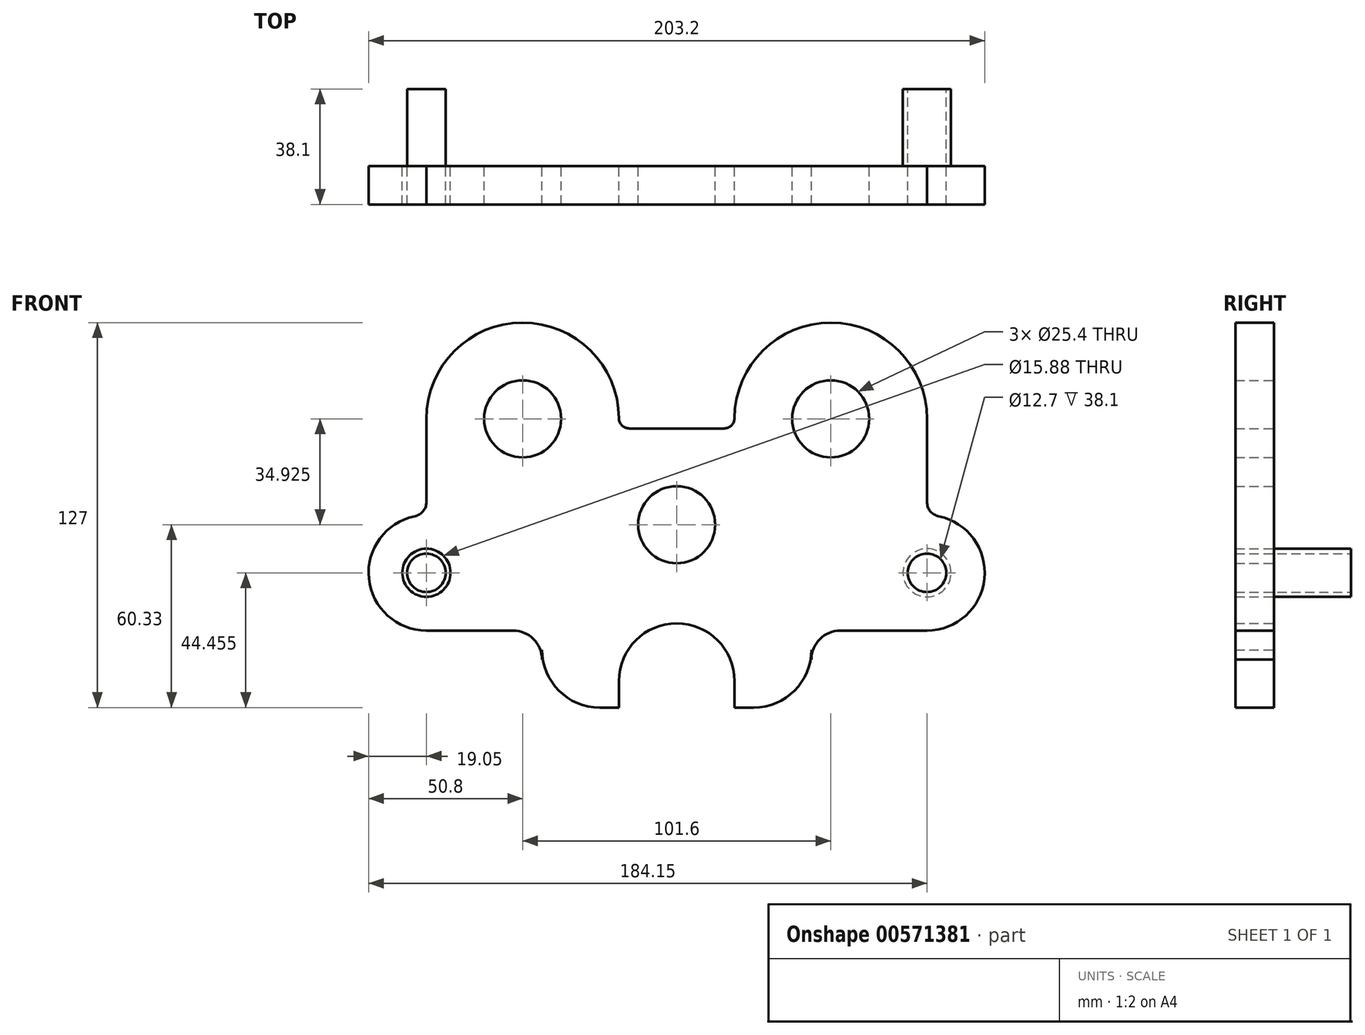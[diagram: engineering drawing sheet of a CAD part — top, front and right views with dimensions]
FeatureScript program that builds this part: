
annotation { "Feature Type Name" : "Feature", "Feature Type Description" : "" }
export const myFeature = defineFeature(function(context is Context, id is Id, definition is map)
    precondition{}
    {
        {
            var Q0;
            Q0=qCreatedBy(makeId("Front.planeOp"),FACE);
            var sketch = newSketch(context, id + "F0", { "sketchPlane" : qUnion([Q0])});
            skArc(sketch, "E0", {"start": v(82.55, 34.93) * mm, "mid": v(50.9, 66.67) * mm, "end": v(19.05, 35.12) * mm});
            skLineSegment(sketch, "E1", {"start": v(82.55, 34.93) * mm, "end": v(82.55, 7.46) * mm});
            skArc(sketch, "E2", {"start": v(82.55, -34.92) * mm, "mid": v(101.5, -17.79) * mm, "end": v(86.36, 2.8) * mm});
            skLineSegment(sketch, "E3", {"start": v(82.55, -34.92) * mm, "end": v(53.98, -34.92) * mm});
            skCircle(sketch, "E4", {"center": v(50.8, 34.93) * mm, "radius": 12.7 * mm});
            skCircle(sketch, "E5", {"center": v(82.55, -15.87) * mm, "radius": 6.35 * mm});
            skLineSegment(sketch, "E6", {"start": v(50.8, 74.41) * mm, "end": v(50.8, -7.1) * mm, "construction": true});
            skPoint(sketch, "E6.startSnap0", {"position": v(50.8, 66.67) * mm});
            skLineSegment(sketch, "E7", {"start": v(72.24, 34.93) * mm, "end": v(7.49, 34.93) * mm, "construction": true});
            skLineSegment(sketch, "E8", {"start": v(82.55, 0) * mm, "end": v(82.55, -56.09) * mm, "construction": true});
            skLineSegment(sketch, "E9", {"start": v(38.27, -15.87) * mm, "end": v(117.37, -15.87) * mm, "construction": true});
            skCircle(sketch, "E10", {"center": v(0, 0) * mm, "radius": 12.7 * mm});
            skLineSegment(sketch, "E11", {"start": v(0, 42.71) * mm, "end": v(0, -64.9) * mm, "construction": true});
            skLineSegment(sketch, "E12", {"start": v(-44.82, 0) * mm, "end": v(29.18, 0) * mm, "construction": true});
            skPoint(sketch, "E13.orphan", {"position": v(0, 34.92) * mm});
            skLineSegment(sketch, "E14", {"start": v(0, 31.75) * mm, "end": v(15.66, 31.75) * mm});
            skLineSegment(sketch, "E15", {"start": v(44.45, -41.27) * mm, "end": v(44.45, -44.45) * mm});
            skLineSegment(sketch, "E16", {"start": v(25.4, -60.32) * mm, "end": v(19.05, -60.32) * mm});
            skLineSegment(sketch, "E17", {"start": v(19.05, -60.32) * mm, "end": v(19.05, -51.59) * mm});
            skPoint(sketch, "E18.visualSharp", {"position": v(19.05, -32.6) * mm});
            skPoint(sketch, "E19.visualSharp", {"position": v(44.45, -60.32) * mm});
            skArc(sketch, "E19.filletArc", {"start": v(25.4, -60.32) * mm, "mid": v(38.87, -54.75) * mm, "end": v(44.45, -41.27) * mm});
            skPoint(sketch, "E20.visualSharp", {"position": v(44.45, -34.92) * mm});
            skArc(sketch, "E20.filletArc", {"start": v(53.98, -34.92) * mm, "mid": v(47.24, -37.71) * mm, "end": v(44.45, -44.45) * mm});
            skPoint(sketch, "E21.visualSharp", {"position": v(82.55, 3.17) * mm});
            skArc(sketch, "E21.filletArc", {"start": v(82.55, 7.46) * mm, "mid": v(83.62, 4.44) * mm, "end": v(86.36, 2.8) * mm});
            skPoint(sketch, "E22.newPointA", {"position": v(19.05, 34.92) * mm});
            skPoint(sketch, "E22.newPointB", {"position": v(7.49, 31.75) * mm});
            skArc(sketch, "E22.filletArc", {"start": v(15.66, 31.75) * mm, "mid": v(18.05, 32.73) * mm, "end": v(19.05, 35.12) * mm});
            skLineSegment(sketch, "E23", {"start": v(-60.5, -47.62) * mm, "end": v(83.9, -47.62) * mm, "construction": true});
            skLineSegment(sketch, "E24.MirrorCS", {"start": v(0, 31.75) * mm, "end": v(-15.66, 31.75) * mm});
            skPoint(sketch, "E25.MirrorP", {"position": v(-7.49, 31.75) * mm});
            skPoint(sketch, "E26.MirrorP", {"position": v(-19.05, 34.92) * mm});
            skArc(sketch, "E27.MirrorCS", {"start": v(-82.55, 34.93) * mm, "mid": v(-50.9, 66.67) * mm, "end": v(-19.05, 35.12) * mm});
            skLineSegment(sketch, "E28.MirrorCS", {"start": v(-82.55, 34.93) * mm, "end": v(-82.55, 7.46) * mm});
            skArc(sketch, "E29.MirrorCS", {"start": v(-82.55, -34.92) * mm, "mid": v(-101.5, -17.79) * mm, "end": v(-86.36, 2.8) * mm});
            skLineSegment(sketch, "E30.MirrorCS", {"start": v(-82.55, -34.93) * mm, "end": v(-53.98, -34.92) * mm});
            skArc(sketch, "E31.MirrorCS", {"start": v(-25.4, -60.32) * mm, "mid": v(-38.87, -54.75) * mm, "end": v(-44.45, -41.27) * mm});
            skLineSegment(sketch, "E32.MirrorCS", {"start": v(-25.4, -60.32) * mm, "end": v(-19.05, -60.32) * mm});
            skLineSegment(sketch, "E33.MirrorCS", {"start": v(-19.05, -60.32) * mm, "end": v(-19.05, -51.59) * mm});
            skPoint(sketch, "E34.newPointA", {"position": v(-86.36, 2.8) * mm});
            skPoint(sketch, "E34.newPointB", {"position": v(-82.55, 7.46) * mm});
            skArc(sketch, "E34.filletArc", {"start": v(-86.36, 2.8) * mm, "mid": v(-83.62, 4.44) * mm, "end": v(-82.55, 7.46) * mm});
            skArc(sketch, "E35.MirrorCS", {"start": v(-53.98, -34.92) * mm, "mid": v(-47.24, -37.71) * mm, "end": v(-44.45, -44.45) * mm});
            skLineSegment(sketch, "E36.MirrorCS", {"start": v(-44.45, -41.27) * mm, "end": v(-44.45, -44.45) * mm});
            skArc(sketch, "E37.MirrorCS", {"start": v(-15.66, 31.75) * mm, "mid": v(-18.05, 32.73) * mm, "end": v(-19.05, 35.12) * mm});
            skCircle(sketch, "E38.MirrorC", {"center": v(-50.8, 34.93) * mm, "radius": 12.7 * mm});
            skCircle(sketch, "E39.MirrorC", {"center": v(-82.55, -15.87) * mm, "radius": 6.35 * mm});
            skArc(sketch, "E40", {"start": v(19.05, -51.59) * mm, "mid": v(0, -32.54) * mm, "end": v(-19.05, -51.59) * mm});
            skLineSegment(sketch, "E41", {"start": v(-101.6, 46.46) * mm, "end": v(-101.6, -66.93) * mm, "construction": true});
            skLineSegment(sketch, "E42", {"start": v(-101.6, -66.93) * mm, "end": v(-101.6, 3.67) * mm, "construction": true});
            skLineSegment(sketch, "E43", {"start": v(-44.45, -4.7) * mm, "end": v(-44.45, -75.32) * mm});
            skLineSegment(sketch, "E44", {"start": v(-17.52, 66.67) * mm, "end": v(-84.96, 66.67) * mm, "construction": true});
            skLineSegment(sketch, "E45", {"start": v(-20.55, -60.32) * mm, "end": v(-66.48, -60.32) * mm, "construction": true});
            skPoint(sketch, "E46.MirrorP", {"position": v(-82.55, 3.17) * mm});
            skArc(sketch, "E47.MirrorCS", {"start": v(-82.55, 7.46) * mm, "mid": v(-83.62, 4.44) * mm, "end": v(-86.36, 2.8) * mm});
            skCircle(sketch, "E48", {"center": v(-82.55, -15.87) * mm, "radius": 7.94 * mm});
            skCircle(sketch, "E49", {"center": v(82.55, -15.87) * mm, "radius": 7.94 * mm});
            skSolve(sketch);
        }
        {
            var Q0;
            Q0=makeQuery(id+"F0.imprint","IMPRINT",FACE,{"disambiguationData":[TD([[makeQuery(id+"F0.imprint","IMPRINT",EDGE,{"derivedFrom":sQuery(id+"F0.wireOp",EDGE,"E0")}),1.0]])]});
            var Q1;
            Q1=makeQuery(id+"F0.imprint","IMPRINT",FACE,{"disambiguationData":[TD([[makeQuery(id+"F0.imprint","IMPRINT",EDGE,{"derivedFrom":sQuery(id+"F0.wireOp",EDGE,"E39.MirrorC")}),1.0]])]});
            var Q2;
            Q2=makeQuery(id+"F0.imprint","IMPRINT",FACE,{"disambiguationData":[TD([[makeQuery(id+"F0.imprint","IMPRINT",EDGE,{"derivedFrom":sQuery(id+"F0.wireOp",EDGE,"E5")}),-1.0]])]});
            extrude(context, id + "F1", {"entities" : qUnion([Q0, Q1, Q2]), "depth" : 12.7 * mm, "offsetDistance" : 25.4 * mm});
        }
        {
            var Q0;
            Q0=makeQuery(id+"F0.imprint","IMPRINT",FACE,{"disambiguationData":[TD([[makeQuery(id+"F0.imprint","IMPRINT",EDGE,{"derivedFrom":sQuery(id+"F0.wireOp",EDGE,"E5")}),-1.0]])]});
            var Q1;
            Q1=makeQuery(id+"F0.imprint","IMPRINT",FACE,{"disambiguationData":[TD([[makeQuery(id+"F0.imprint","IMPRINT",EDGE,{"derivedFrom":sQuery(id+"F0.wireOp",EDGE,"E39.MirrorC")}),1.0]])]});
            extrude(context, id + "F2", {"entities" : qUnion([Q0, Q1]), "operationType" : NewBodyOperationType.ADD, "oppositeDirection" : true, "depth" : 25.4 * mm, "offsetDistance" : 25.4 * mm});
        }
    });
